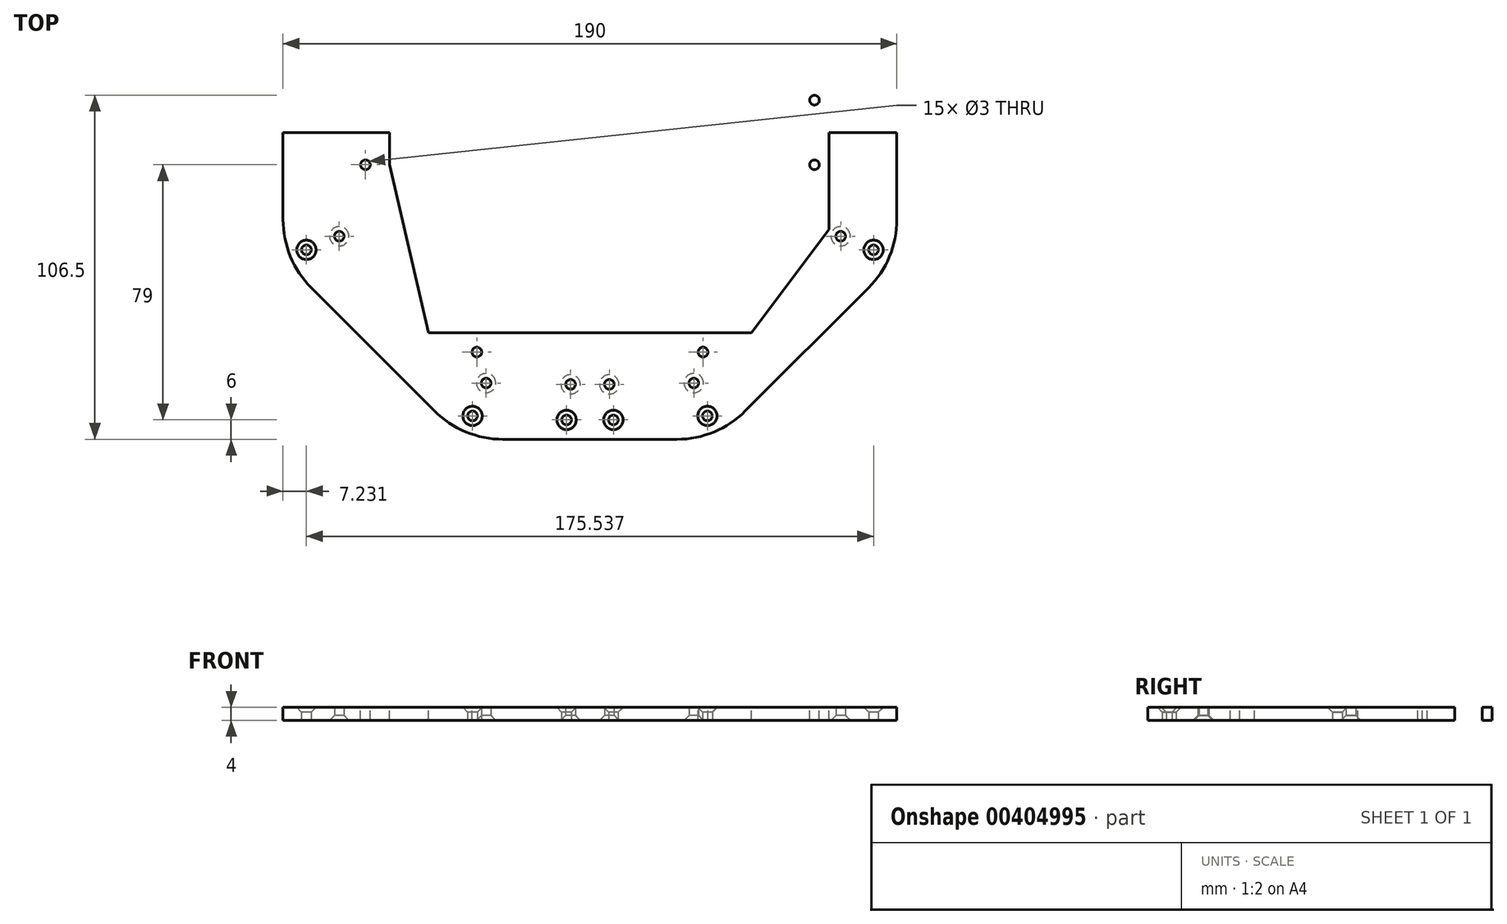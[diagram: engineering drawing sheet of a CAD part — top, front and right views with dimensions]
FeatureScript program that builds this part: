
annotation { "Feature Type Name" : "Feature", "Feature Type Description" : "" }
export const myFeature = defineFeature(function(context is Context, id is Id, definition is map)
    precondition{}
    {
        {
            var Q0;
            Q0=qCreatedBy(makeId("Top.planeOp"),FACE);
            var sketch = newSketch(context, id + "F0", { "sketchPlane" : qUnion([Q0])});
            skCircle(sketch, "E0.cCircle", {"center": v(0, 0) * mm, "radius": 95 * mm, "construction": true});
            skLineSegment(sketch, "E0.0", {"start": v(39.35, -95) * mm, "end": v(-39.35, -95) * mm});
            skLineSegment(sketch, "E0.1", {"start": v(-39.35, -95) * mm, "end": v(-95, -39.35) * mm});
            skLineSegment(sketch, "E0.2", {"start": v(-95, -39.35) * mm, "end": v(-95, 39.35) * mm});
            skLineSegment(sketch, "E0.3", {"start": v(-95, 39.35) * mm, "end": v(-39.35, 95) * mm});
            skLineSegment(sketch, "E0.4", {"start": v(-39.35, 95) * mm, "end": v(39.35, 95) * mm});
            skLineSegment(sketch, "E0.5", {"start": v(39.35, 95) * mm, "end": v(95, 39.35) * mm});
            skLineSegment(sketch, "E0.6", {"start": v(95, 39.35) * mm, "end": v(95, -39.35) * mm});
            skLineSegment(sketch, "E0.7", {"start": v(95, -39.35) * mm, "end": v(39.35, -95) * mm});
            skLineSegment(sketch, "E1", {"start": v(0, 0) * mm, "end": v(-95, 0) * mm});
            skLineSegment(sketch, "E2", {"start": v(0, 0) * mm, "end": v(95, 0) * mm});
            skLineSegment(sketch, "E3", {"start": v(-95, -39.35) * mm, "end": v(0, 0) * mm, "construction": true});
            skCircle(sketch, "E4", {"center": v(-87.77, -36.35) * mm, "radius": 1.5 * mm});
            skCircle(sketch, "E5.1.0", {"center": v(-36.35, -87.77) * mm, "radius": 1.5 * mm});
            skCircle(sketch, "E5.2.0", {"center": v(36.35, -87.77) * mm, "radius": 1.5 * mm});
            skCircle(sketch, "E5.3.0", {"center": v(87.77, -36.35) * mm, "radius": 1.5 * mm});
            skCircle(sketch, "E5.4.0", {"center": v(87.77, 36.35) * mm, "radius": 1.5 * mm});
            skCircle(sketch, "E5.5.0", {"center": v(36.35, 87.77) * mm, "radius": 1.5 * mm});
            skCircle(sketch, "E5.6.0", {"center": v(-36.35, 87.77) * mm, "radius": 1.5 * mm});
            skCircle(sketch, "E5.7.0", {"center": v(-87.77, 36.35) * mm, "radius": 1.5 * mm});
            skCircle(sketch, "E6", {"center": v(-77.6, -32.15) * mm, "radius": 1.5 * mm});
            skLineSegment(sketch, "E7", {"start": v(0, 0) * mm, "end": v(0, -89) * mm, "construction": true});
            skLineSegment(sketch, "E8", {"start": v(0, -89) * mm, "end": v(-7.25, -89) * mm, "construction": true});
            skLineSegment(sketch, "E9", {"start": v(0, -89) * mm, "end": v(7.25, -89) * mm, "construction": true});
            skCircle(sketch, "E10", {"center": v(-7.25, -89) * mm, "radius": 1.5 * mm});
            skCircle(sketch, "E11", {"center": v(7.25, -89) * mm, "radius": 1.5 * mm});
            skCircle(sketch, "E12.1.0", {"center": v(7.25, 89) * mm, "radius": 1.5 * mm});
            skCircle(sketch, "E12.1.1", {"center": v(-7.25, 89) * mm, "radius": 1.5 * mm});
            skCircle(sketch, "E13.1.0", {"center": v(-32.15, -77.6) * mm, "radius": 1.5 * mm});
            skCircle(sketch, "E13.2.0", {"center": v(32.15, -77.6) * mm, "radius": 1.5 * mm});
            skCircle(sketch, "E13.3.0", {"center": v(77.6, -32.15) * mm, "radius": 1.5 * mm});
            skCircle(sketch, "E13.4.0", {"center": v(77.6, 32.15) * mm, "radius": 1.5 * mm});
            skCircle(sketch, "E13.5.0", {"center": v(32.15, 77.6) * mm, "radius": 1.5 * mm});
            skCircle(sketch, "E13.6.0", {"center": v(-32.15, 77.6) * mm, "radius": 1.5 * mm});
            skCircle(sketch, "E13.7.0", {"center": v(-77.6, 32.15) * mm, "radius": 1.5 * mm});
            skLineSegment(sketch, "E14", {"start": v(0, -78) * mm, "end": v(-6, -78) * mm, "construction": true});
            skLineSegment(sketch, "E15", {"start": v(0, -78) * mm, "end": v(6, -78) * mm, "construction": true});
            skCircle(sketch, "E16", {"center": v(-6, -78) * mm, "radius": 1.5 * mm});
            skCircle(sketch, "E17", {"center": v(6, -78) * mm, "radius": 1.5 * mm});
            skCircle(sketch, "E18.1.0", {"center": v(-6, 78) * mm, "radius": 1.5 * mm});
            skCircle(sketch, "E18.1.1", {"center": v(6, 78) * mm, "radius": 1.5 * mm});
            skSolve(sketch);
        }
        {
            var Q0;
            {var subQ1=sQuery(id+"F0.wireOp",EDGE,"E0.3");Q0=makeQuery(id+"F0.imprint","IMPRINT",FACE,{"disambiguationData":[TD([[makeQuery(id+"F0.imprint","IMPRINT",EDGE,{"derivedFrom":subQ1}),-1.0]])]});}
            var Q1;
            {var subQ1=sQuery(id+"F0.wireOp",EDGE,"E0.3");Q1=makeQuery(id+"F0.imprint","IMPRINT",FACE,{"disambiguationData":[TD([[makeQuery(id+"F0.imprint","IMPRINT",EDGE,{"derivedFrom":subQ1}),-1.0]])]});}
            extrude(context, id + "F1", {"entities" : qUnion([Q0, Q1]), "depth" : 4 * mm});
        }
        {
            var Q0;
            Q0=makeQuery(id+"F0.imprint","IMPRINT",FACE,{"disambiguationData":[TD([[makeQuery(id+"F0.imprint","IMPRINT",EDGE,{"derivedFrom":sQuery(id+"F0.wireOp",EDGE,"E0.0")}),-1.0]])]});
            extrude(context, id + "F2", {"entities" : qUnion([Q0]), "depth" : 4 * mm});
        }
        {
            var Q0;
            Q0=makeQuery(id+"F2.opExtrude","SWEPT_EDGE",EDGE,{"disambiguationData":[OSD([sQuery(id+"F0.wireOp",EDGE,"E0.1"),sQuery(id+"F0.wireOp",EDGE,"E0.2")])]});
            var Q1;
            Q1=makeQuery(id+"F2.opExtrude","SWEPT_EDGE",EDGE,{"disambiguationData":[OSD([sQuery(id+"F0.wireOp",EDGE,"E0.6"),sQuery(id+"F0.wireOp",EDGE,"E0.7")])]});
            var Q2;
            Q2=makeQuery(id+"F1.opExtrude","SWEPT_EDGE",EDGE,{"disambiguationData":[OSD([sQuery(id+"F0.wireOp",EDGE,"E0.5"),sQuery(id+"F0.wireOp",EDGE,"E0.6")])]});
            var Q3;
            Q3=makeQuery(id+"F1.opExtrude","SWEPT_EDGE",EDGE,{"disambiguationData":[OSD([sQuery(id+"F0.wireOp",EDGE,"E0.4"),sQuery(id+"F0.wireOp",EDGE,"E0.5")])]});
            var Q4;
            Q4=makeQuery(id+"F1.opExtrude","SWEPT_EDGE",EDGE,{"disambiguationData":[OSD([sQuery(id+"F0.wireOp",EDGE,"E0.3"),sQuery(id+"F0.wireOp",EDGE,"E0.4")])]});
            var Q5;
            Q5=makeQuery(id+"F1.opExtrude","SWEPT_EDGE",EDGE,{"disambiguationData":[OSD([sQuery(id+"F0.wireOp",EDGE,"E0.2"),sQuery(id+"F0.wireOp",EDGE,"E0.3")])]});
            var Q6;
            Q6=makeQuery(id+"F2.opExtrude","SWEPT_EDGE",EDGE,{"disambiguationData":[OSD([sQuery(id+"F0.wireOp",EDGE,"E0.0"),sQuery(id+"F0.wireOp",EDGE,"E0.1")])]});
            var Q7;
            Q7=makeQuery(id+"F2.opExtrude","SWEPT_EDGE",EDGE,{"disambiguationData":[OSD([sQuery(id+"F0.wireOp",EDGE,"E0.0"),sQuery(id+"F0.wireOp",EDGE,"E0.7")])]});
            fillet(context, id + "F3", {"entities" : qUnion([Q0, Q1, Q2, Q3, Q4, Q5, Q6, Q7]), "radius" : 30 * mm, "tangentPropagation" : true, "allowEdgeOverflow" : false});
        }
        {
            var Q0;
            Q0=makeQuery(id+"F1.opExtrude","CAP_FACE",FACE,{"disambiguationData":[OSD([sQuery(id+"F0.wireOp",EDGE,"E0.2"),sQuery(id+"F0.wireOp",EDGE,"E0.3"),sQuery(id+"F0.wireOp",EDGE,"E0.4"),sQuery(id+"F0.wireOp",EDGE,"E0.5"),sQuery(id+"F0.wireOp",EDGE,"E0.6"),sQuery(id+"F0.wireOp",EDGE,"FWvXgzkW-92Ol-D1nR-HL31-QDwloOWlVPkl"),sQuery(id+"F0.wireOp",EDGE,"KB5lrl97-oh6M-4FKn-tIKZ-oEGIWaDHRA87"),sQuery(id+"F0.wireOp",EDGE,"1a06ab86-549c-4c23-92a1-abe76b86ff2b"),sQuery(id+"F0.wireOp",EDGE,"3b6d9c79-dd86-4e60-94f1-2d74a6fdfb3c.4.1"),sQuery(id+"F0.wireOp",EDGE,"3b6d9c79-dd86-4e60-94f1-2d74a6fdfb3c.5.0"),sQuery(id+"F0.wireOp",EDGE,"3b6d9c79-dd86-4e60-94f1-2d74a6fdfb3c.5.1"),sQuery(id+"F0.wireOp",EDGE,"3b6d9c79-dd86-4e60-94f1-2d74a6fdfb3c.6.0"),sQuery(id+"F0.wireOp",EDGE,"3b6d9c79-dd86-4e60-94f1-2d74a6fdfb3c.6.1"),sQuery(id+"F0.wireOp",EDGE,"3b6d9c79-dd86-4e60-94f1-2d74a6fdfb3c.7.0"),sQuery(id+"F0.wireOp",EDGE,"3b6d9c79-dd86-4e60-94f1-2d74a6fdfb3c.7.1")])],"isStart":false});
            var sketch = newSketch(context, id + "F4", { "sketchPlane" : qUnion([Q0])});
            skLineSegment(sketch, "E19.bottom", {"start": v(-35, 68) * mm, "end": v(35, 68) * mm, "construction": true});
            skLineSegment(sketch, "E19.top", {"start": v(-35, -68) * mm, "end": v(35, -68) * mm, "construction": true});
            skLineSegment(sketch, "E19.left", {"start": v(-35, 68) * mm, "end": v(-35, -68) * mm, "construction": true});
            skLineSegment(sketch, "E19.right", {"start": v(35, 68) * mm, "end": v(35, -68) * mm, "construction": true});
            skPoint(sketch, "E19.middle", {"position": v(0, 0) * mm});
            skCircle(sketch, "E20", {"center": v(-35, 68) * mm, "radius": 1.5 * mm});
            skCircle(sketch, "E21", {"center": v(35, 68) * mm, "radius": 1.5 * mm});
            skCircle(sketch, "E22", {"center": v(35, -68) * mm, "radius": 1.5 * mm});
            skCircle(sketch, "E23", {"center": v(-35, -68) * mm, "radius": 1.5 * mm});
            skSolve(sketch);
        }
        {
            var Q0;
            Q0=makeQuery(id+"F4.imprint","IMPRINT",FACE,{"disambiguationData":[TD([[makeQuery(id+"F4.imprint","IMPRINT",EDGE,{"derivedFrom":sQuery(id+"F4.wireOp",EDGE,"E20")}),1.0]])]});
            var Q1;
            Q1=makeQuery(id+"F4.imprint","IMPRINT",FACE,{"disambiguationData":[TD([[makeQuery(id+"F4.imprint","IMPRINT",EDGE,{"derivedFrom":sQuery(id+"F4.wireOp",EDGE,"E21")}),1.0]])]});
            var Q2;
            Q2=makeQuery(id+"F4.imprint","IMPRINT",FACE,{"disambiguationData":[TD([[makeQuery(id+"F4.imprint","IMPRINT",EDGE,{"derivedFrom":sQuery(id+"F4.wireOp",EDGE,"E22")}),1.0]])]});
            var Q3;
            Q3=makeQuery(id+"F4.imprint","IMPRINT",FACE,{"disambiguationData":[TD([[makeQuery(id+"F4.imprint","IMPRINT",EDGE,{"derivedFrom":sQuery(id+"F4.wireOp",EDGE,"E23")}),1.0]])]});
            extrude(context, id + "F5", {"entities" : qUnion([Q0, Q1, Q2, Q3]), "operationType" : NewBodyOperationType.REMOVE, "oppositeDirection" : true, "depth" : 25 * mm});
        }
        {
            var Q0;
            Q0=makeQuery(id+"F1.opExtrude","CAP_FACE",FACE,{"disambiguationData":[OSD([sQuery(id+"F0.wireOp",EDGE,"E0.2"),sQuery(id+"F0.wireOp",EDGE,"E0.3"),sQuery(id+"F0.wireOp",EDGE,"E0.4"),sQuery(id+"F0.wireOp",EDGE,"E0.5"),sQuery(id+"F0.wireOp",EDGE,"E0.6"),sQuery(id+"F0.wireOp",EDGE,"FWvXgzkW-92Ol-D1nR-HL31-QDwloOWlVPkl"),sQuery(id+"F0.wireOp",EDGE,"KB5lrl97-oh6M-4FKn-tIKZ-oEGIWaDHRA87"),sQuery(id+"F0.wireOp",EDGE,"ce847c22-4656-4ac6-8dae-eb3496d83a06.7.0"),sQuery(id+"F0.wireOp",EDGE,"ce847c22-4656-4ac6-8dae-eb3496d83a06.7.1"),sQuery(id+"F0.wireOp",EDGE,"2ddf77b3-c7c5-494c-ac41-90231f072106.1.0"),sQuery(id+"F0.wireOp",EDGE,"2ddf77b3-c7c5-494c-ac41-90231f072106.1.1"),sQuery(id+"F0.wireOp",EDGE,"2ddf77b3-c7c5-494c-ac41-90231f072106.1.2"),sQuery(id+"F0.wireOp",EDGE,"2ddf77b3-c7c5-494c-ac41-90231f072106.1.3"),sQuery(id+"F0.wireOp",EDGE,"2ddf77b3-c7c5-494c-ac41-90231f072106.2.0"),sQuery(id+"F0.wireOp",EDGE,"2ddf77b3-c7c5-494c-ac41-90231f072106.2.1"),sQuery(id+"F0.wireOp",EDGE,"2ddf77b3-c7c5-494c-ac41-90231f072106.2.2"),sQuery(id+"F0.wireOp",EDGE,"2ddf77b3-c7c5-494c-ac41-90231f072106.2.3"),sQuery(id+"F0.wireOp",EDGE,"2ddf77b3-c7c5-494c-ac41-90231f072106.3.0"),sQuery(id+"F0.wireOp",EDGE,"2ddf77b3-c7c5-494c-ac41-90231f072106.3.1"),sQuery(id+"F0.wireOp",EDGE,"2ddf77b3-c7c5-494c-ac41-90231f072106.3.2"),sQuery(id+"F0.wireOp",EDGE,"2ddf77b3-c7c5-494c-ac41-90231f072106.3.3"),sQuery(id+"F0.wireOp",EDGE,"2ddf77b3-c7c5-494c-ac41-90231f072106.4.0"),sQuery(id+"F0.wireOp",EDGE,"2ddf77b3-c7c5-494c-ac41-90231f072106.4.1")])],"isStart":false});
            var sketch = newSketch(context, id + "F6", { "sketchPlane" : qUnion([Q0])});
            skLineSegment(sketch, "E24", {"start": v(-50, 63) * mm, "end": v(50, 63) * mm});
            skLineSegment(sketch, "E25", {"start": v(50, 63) * mm, "end": v(50, -62) * mm});
            skLineSegment(sketch, "E26.top", {"start": v(-50, -62) * mm, "end": v(50, -62) * mm});
            skLineSegment(sketch, "E26.left", {"start": v(-50, 63) * mm, "end": v(-50, -62) * mm});
            skLineSegment(sketch, "E27", {"start": v(-35, 68) * mm, "end": v(35, 68) * mm});
            skLineSegment(sketch, "E28", {"start": v(0, 68) * mm, "end": v(0, 63) * mm});
            skLineSegment(sketch, "E29", {"start": v(50, -62) * mm, "end": v(74, -30) * mm});
            skLineSegment(sketch, "E30", {"start": v(74, -30) * mm, "end": v(74, 0) * mm});
            skLineSegment(sketch, "E31", {"start": v(74, 0) * mm, "end": v(50, 0) * mm});
            skLineSegment(sketch, "E32", {"start": v(0, 0) * mm, "end": v(-69.5, 0) * mm});
            skLineSegment(sketch, "E33", {"start": v(-69.5, 0) * mm, "end": v(-69.5, -10) * mm});
            skLineSegment(sketch, "E34", {"start": v(-69.5, 0) * mm, "end": v(-69.5, 10) * mm});
            skCircle(sketch, "E35", {"center": v(-69.5, 10) * mm, "radius": 1.5 * mm});
            skCircle(sketch, "E36", {"center": v(-69.5, -10) * mm, "radius": 1.5 * mm});
            skLineSegment(sketch, "E37", {"start": v(0, 0) * mm, "end": v(0, -20.98) * mm, "construction": true});
            skCircle(sketch, "E38.MirrorC", {"center": v(69.5, 10) * mm, "radius": 1.5 * mm});
            skCircle(sketch, "E39.MirrorC", {"center": v(69.5, -10) * mm, "radius": 1.5 * mm});
            skLineSegment(sketch, "E40", {"start": v(-50, 63) * mm, "end": v(-62, 10) * mm});
            skLineSegment(sketch, "E41", {"start": v(-62, 10) * mm, "end": v(-62, 0) * mm});
            skLineSegment(sketch, "E42", {"start": v(-62, 0) * mm, "end": v(-62, -10) * mm});
            skLineSegment(sketch, "E43", {"start": v(-62, -10) * mm, "end": v(-50, -62) * mm});
            skLineSegment(sketch, "E44", {"start": v(50, 63) * mm, "end": v(62, 10) * mm});
            skLineSegment(sketch, "E45", {"start": v(62, 10) * mm, "end": v(62, 0) * mm});
            skSolve(sketch);
        }
        {
            var Q0;
            {var subQ1=sQuery(id+"F6.wireOp",EDGE,"E24");var subQ16=makeQuery(id+"F6.imprint","IMPRINT",VERTEX,{"derivedFrom":subQ1});Q0=makeQuery(id+"F6.imprint","IMPRINT",FACE,{"disambiguationData":[TD([[makeQuery(id+"F6.imprint","IMPRINT",EDGE,{"disambiguationData":[TD([[subQ16,1.0]])],"derivedFrom":subQ1}),-1.0]])]});}
            var Q1;
            {var subQ10=sQuery(id+"F6.wireOp",EDGE,"E26.top");Q1=makeQuery(id+"F6.imprint","IMPRINT",FACE,{"disambiguationData":[TD([[makeQuery(id+"F6.imprint","IMPRINT",EDGE,{"derivedFrom":subQ10}),1.0]])]});}
            var Q2;
            Q2=makeQuery(id+"F6.imprint","IMPRINT",FACE,{"disambiguationData":[TD([[makeQuery(id+"F6.imprint","IMPRINT",EDGE,{"derivedFrom":sQuery(id+"F6.wireOp",EDGE,"E36")}),1.0]])]});
            var Q3;
            Q3=makeQuery(id+"F6.imprint","IMPRINT",FACE,{"disambiguationData":[TD([[makeQuery(id+"F6.imprint","IMPRINT",EDGE,{"derivedFrom":sQuery(id+"F6.wireOp",EDGE,"E35")}),1.0]])]});
            var Q4;
            Q4=makeQuery(id+"F6.imprint","IMPRINT",FACE,{"disambiguationData":[TD([[makeQuery(id+"F6.imprint","IMPRINT",EDGE,{"derivedFrom":sQuery(id+"F6.wireOp",EDGE,"E38.MirrorC")}),-1.0]])]});
            var Q5;
            {var subQ1=sQuery(id+"F6.wireOp",EDGE,"E29");Q5=makeQuery(id+"F6.imprint","IMPRINT",FACE,{"disambiguationData":[TD([[makeQuery(id+"F6.imprint","IMPRINT",EDGE,{"derivedFrom":subQ1}),1.0]])]});}
            var Q6;
            Q6=makeQuery(id+"F6.imprint","IMPRINT",FACE,{"disambiguationData":[TD([[makeQuery(id+"F6.imprint","IMPRINT",EDGE,{"derivedFrom":sQuery(id+"F6.wireOp",EDGE,"E39.MirrorC")}),-1.0]])]});
            var Q7;
            {var subQ0=sQuery(id+"F6.wireOp",EDGE,"E40");Q7=makeQuery(id+"F6.imprint","IMPRINT",FACE,{"disambiguationData":[TD([[makeQuery(id+"F6.imprint","IMPRINT",EDGE,{"derivedFrom":subQ0}),1.0]])]});}
            var Q8;
            {var subQ4=sQuery(id+"F6.wireOp",EDGE,"E42");Q8=makeQuery(id+"F6.imprint","IMPRINT",FACE,{"disambiguationData":[TD([[makeQuery(id+"F6.imprint","IMPRINT",EDGE,{"derivedFrom":subQ4}),1.0]])]});}
            var Q9;
            {var subQ0=sQuery(id+"F6.wireOp",EDGE,"E44");Q9=makeQuery(id+"F6.imprint","IMPRINT",FACE,{"disambiguationData":[TD([[makeQuery(id+"F6.imprint","IMPRINT",EDGE,{"derivedFrom":subQ0}),-1.0]])]});}
            extrude(context, id + "F7", {"entities" : qUnion([Q0, Q1, Q2, Q3, Q4, Q5, Q6, Q7, Q8, Q9]), "operationType" : NewBodyOperationType.REMOVE, "oppositeDirection" : true, "depth" : 25 * mm});
        }
        {
            var Q0;
            Q0=makeQuery(id+"F5.boolean.opBoolean","COPY",EDGE,{"derivedFrom":makeQuery(id+"F5.opExtrude","CAP_EDGE",EDGE,{"disambiguationData":[OSD([sQuery(id+"F4.wireOp",EDGE,"E20")])],"isStart":true})});
            var Q1;
            Q1=makeQuery(id+"F5.boolean.opBoolean","COPY",EDGE,{"derivedFrom":makeQuery(id+"F5.opExtrude","CAP_EDGE",EDGE,{"disambiguationData":[OSD([sQuery(id+"F4.wireOp",EDGE,"E21")])],"isStart":true})});
            var Q2;
            Q2=makeQuery(id+"F5.boolean.opBoolean","COPY",EDGE,{"derivedFrom":makeQuery(id+"F5.opExtrude","CAP_EDGE",EDGE,{"disambiguationData":[OSD([sQuery(id+"F4.wireOp",EDGE,"E23")])],"isStart":true})});
            var Q3;
            Q3=makeQuery(id+"F5.boolean.opBoolean","COPY",EDGE,{"derivedFrom":makeQuery(id+"F5.opExtrude","CAP_EDGE",EDGE,{"disambiguationData":[OSD([sQuery(id+"F4.wireOp",EDGE,"E22")])],"isStart":true})});
            var Q4;
            Q4=makeQuery(id+"F2.opExtrude","CAP_EDGE",EDGE,{"disambiguationData":[OSD([sQuery(id+"F0.wireOp",EDGE,"E5.2.0")])],"isStart":false});
            var Q5;
            Q5=makeQuery(id+"F2.opExtrude","CAP_EDGE",EDGE,{"disambiguationData":[OSD([sQuery(id+"F0.wireOp",EDGE,"E11")])],"isStart":false});
            var Q6;
            Q6=makeQuery(id+"F2.opExtrude","CAP_EDGE",EDGE,{"disambiguationData":[OSD([sQuery(id+"F0.wireOp",EDGE,"E10")])],"isStart":false});
            var Q7;
            Q7=makeQuery(id+"F2.opExtrude","CAP_EDGE",EDGE,{"disambiguationData":[OSD([sQuery(id+"F0.wireOp",EDGE,"E5.1.0")])],"isStart":false});
            var Q8;
            Q8=makeQuery(id+"F2.opExtrude","CAP_EDGE",EDGE,{"disambiguationData":[OSD([sQuery(id+"F0.wireOp",EDGE,"E4")])],"isStart":false});
            var Q9;
            Q9=makeQuery(id+"F1.opExtrude","CAP_EDGE",EDGE,{"disambiguationData":[OSD([sQuery(id+"F0.wireOp",EDGE,"E5.7.0")])],"isStart":false});
            var Q10;
            Q10=makeQuery(id+"F1.opExtrude","CAP_EDGE",EDGE,{"disambiguationData":[OSD([sQuery(id+"F0.wireOp",EDGE,"E5.6.0")])],"isStart":false});
            var Q11;
            Q11=makeQuery(id+"F1.opExtrude","CAP_EDGE",EDGE,{"disambiguationData":[OSD([sQuery(id+"F0.wireOp",EDGE,"E12.1.1")])],"isStart":false});
            var Q12;
            Q12=makeQuery(id+"F1.opExtrude","CAP_EDGE",EDGE,{"disambiguationData":[OSD([sQuery(id+"F0.wireOp",EDGE,"E12.1.0")])],"isStart":false});
            var Q13;
            Q13=makeQuery(id+"F1.opExtrude","CAP_EDGE",EDGE,{"disambiguationData":[OSD([sQuery(id+"F0.wireOp",EDGE,"E5.5.0")])],"isStart":false});
            var Q14;
            Q14=makeQuery(id+"F1.opExtrude","CAP_EDGE",EDGE,{"disambiguationData":[OSD([sQuery(id+"F0.wireOp",EDGE,"E5.4.0")])],"isStart":false});
            var Q15;
            Q15=makeQuery(id+"F2.opExtrude","CAP_EDGE",EDGE,{"disambiguationData":[OSD([sQuery(id+"F0.wireOp",EDGE,"E5.3.0")])],"isStart":false});
            var Q16;
            Q16=makeQuery(id+"F2.opExtrude","CAP_EDGE",EDGE,{"disambiguationData":[OSD([sQuery(id+"F0.wireOp",EDGE,"E6")])],"isStart":true});
            var Q17;
            Q17=makeQuery(id+"F2.opExtrude","CAP_EDGE",EDGE,{"disambiguationData":[OSD([sQuery(id+"F0.wireOp",EDGE,"E13.1.0")])],"isStart":true});
            var Q18;
            Q18=makeQuery(id+"F2.opExtrude","CAP_EDGE",EDGE,{"disambiguationData":[OSD([sQuery(id+"F0.wireOp",EDGE,"E16")])],"isStart":true});
            var Q19;
            Q19=makeQuery(id+"F2.opExtrude","CAP_EDGE",EDGE,{"disambiguationData":[OSD([sQuery(id+"F0.wireOp",EDGE,"E17")])],"isStart":true});
            var Q20;
            Q20=makeQuery(id+"F2.opExtrude","CAP_EDGE",EDGE,{"disambiguationData":[OSD([sQuery(id+"F0.wireOp",EDGE,"E13.2.0")])],"isStart":true});
            var Q21;
            Q21=makeQuery(id+"F2.opExtrude","CAP_EDGE",EDGE,{"disambiguationData":[OSD([sQuery(id+"F0.wireOp",EDGE,"E13.3.0")])],"isStart":true});
            var Q22;
            Q22=makeQuery(id+"F1.opExtrude","CAP_EDGE",EDGE,{"disambiguationData":[OSD([sQuery(id+"F0.wireOp",EDGE,"E13.7.0")])],"isStart":true});
            var Q23;
            Q23=makeQuery(id+"F1.opExtrude","CAP_EDGE",EDGE,{"disambiguationData":[OSD([sQuery(id+"F0.wireOp",EDGE,"E13.4.0")])],"isStart":true});
            var Q24;
            Q24=makeQuery(id+"F1.opExtrude","CAP_EDGE",EDGE,{"disambiguationData":[OSD([sQuery(id+"F0.wireOp",EDGE,"E13.5.0")])],"isStart":true});
            var Q25;
            Q25=makeQuery(id+"F1.opExtrude","CAP_EDGE",EDGE,{"disambiguationData":[OSD([sQuery(id+"F0.wireOp",EDGE,"E18.1.1")])],"isStart":true});
            var Q26;
            Q26=makeQuery(id+"F1.opExtrude","CAP_EDGE",EDGE,{"disambiguationData":[OSD([sQuery(id+"F0.wireOp",EDGE,"E18.1.0")])],"isStart":true});
            var Q27;
            Q27=makeQuery(id+"F1.opExtrude","CAP_EDGE",EDGE,{"disambiguationData":[OSD([sQuery(id+"F0.wireOp",EDGE,"E13.6.0")])],"isStart":true});
            var Q28;
            Q28=makeQuery(id+"F7.boolean.opBoolean","COPY",EDGE,{"derivedFrom":makeQuery(id+"F7.opExtrude","CAP_EDGE",EDGE,{"disambiguationData":[OSD([sQuery(id+"F6.wireOp",EDGE,"E35")])],"isStart":true})});
            var Q29;
            Q29=makeQuery(id+"F7.boolean.opBoolean","COPY",EDGE,{"derivedFrom":makeQuery(id+"F7.opExtrude","CAP_EDGE",EDGE,{"disambiguationData":[OSD([sQuery(id+"F6.wireOp",EDGE,"E36")])],"isStart":true})});
            var Q30;
            Q30=makeQuery(id+"F7.boolean.opBoolean","COPY",EDGE,{"derivedFrom":makeQuery(id+"F7.opExtrude","CAP_EDGE",EDGE,{"disambiguationData":[OSD([sQuery(id+"F6.wireOp",EDGE,"E38.MirrorC")])],"isStart":true})});
            chamfer(context, id + "F8", {"entities" : qUnion([Q0, Q1, Q2, Q3, Q4, Q5, Q6, Q7, Q8, Q9, Q10, Q11, Q12, Q13, Q14, Q15, Q16, Q17, Q18, Q19, Q20, Q21, Q22, Q23, Q24, Q25, Q26, Q27, Q28, Q29, Q30]), "width" : 1.5 * mm, "tangentPropagation" : true});
        }
    });
